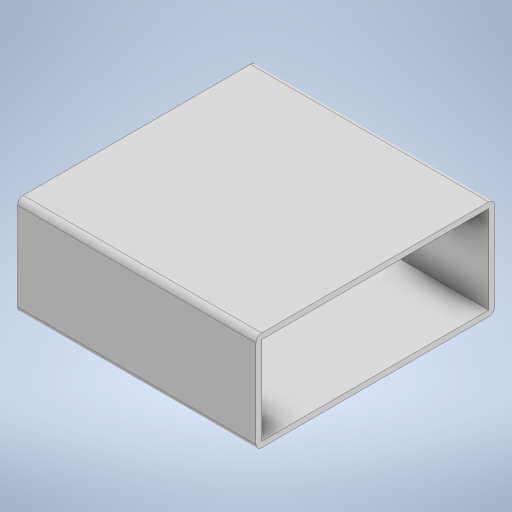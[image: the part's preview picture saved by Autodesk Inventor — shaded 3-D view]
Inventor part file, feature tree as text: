
AUTODESK INVENTOR PART (.ipt)
format: ipt  version: 2023 (Build 270158000, 158)  size: 543,232 bytes
history: native  units: mm
features: extrude x4, sketch x4, fillet x1
ambient origin geometry x8: Origin, YZ Plane, XZ Plane, XY Plane, X Axis, Y Axis, Z Axis, Center Point
bodies: Solide1 (feature_tree)
feature tree (9):
  extrude  "Extrusion1"  Depth=84.0mm
  extrude  "Extrusion2"  Depth=84.0mm
  extrude  "Extrusion3"  Depth=2.0mm TaperAngle=0.0deg
  fillet  "Congé1"  Radius=2.0mm
  extrude  "Extrusion4"  Depth=2.0mm
  sketch  "Esquisse1"
  sketch  "Esquisse2"
  sketch  "Esquisse3"
  sketch  "Esquisse5"
